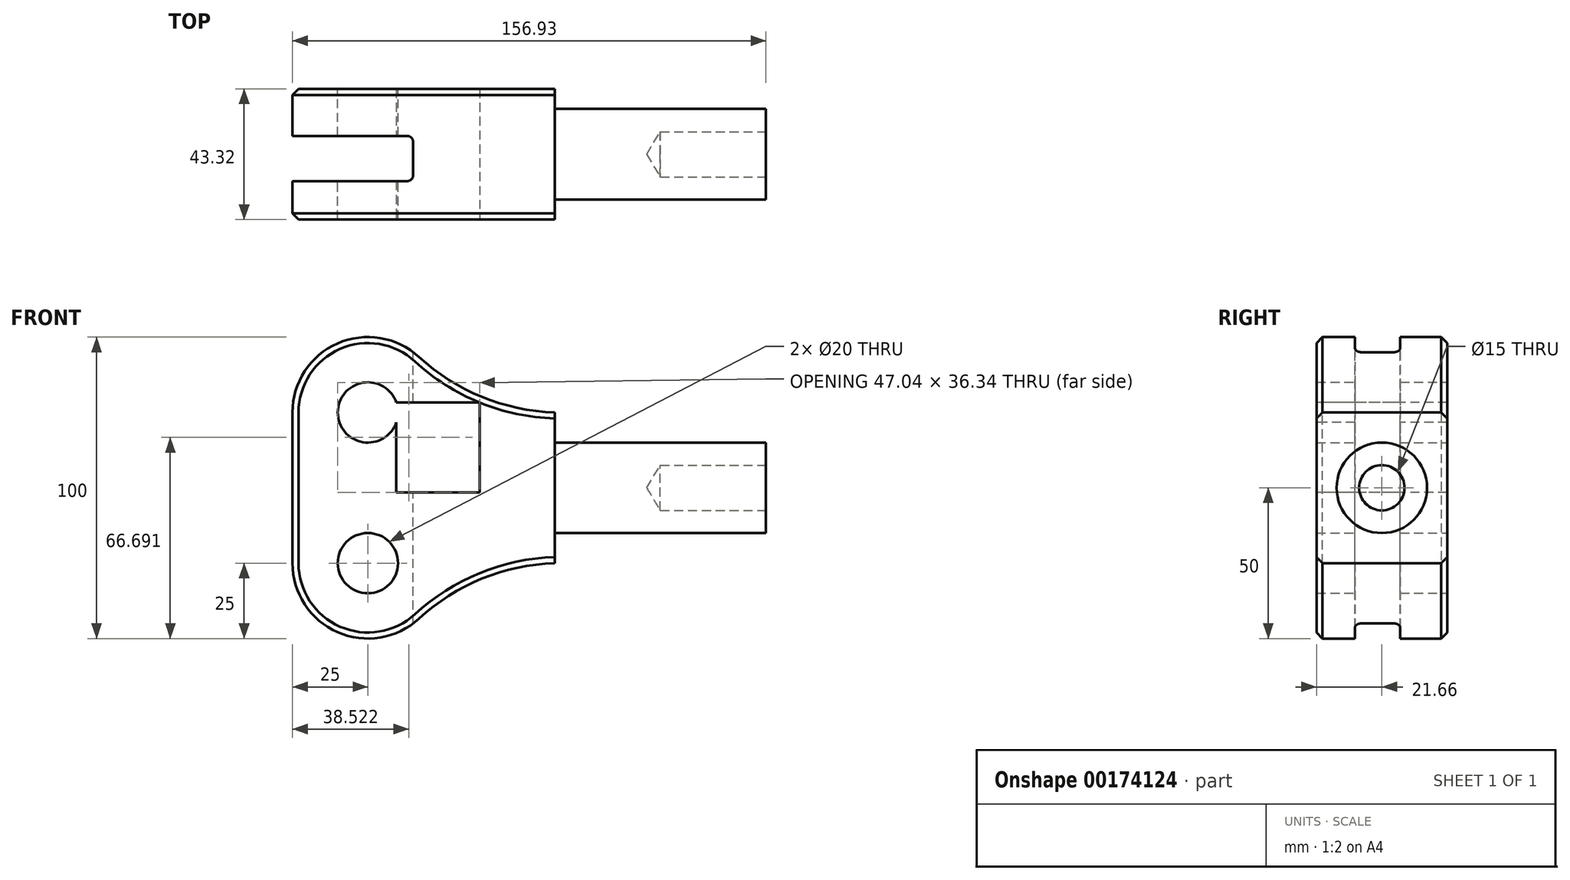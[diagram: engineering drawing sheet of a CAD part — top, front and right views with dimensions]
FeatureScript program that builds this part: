
annotation { "Feature Type Name" : "Feature", "Feature Type Description" : "" }
export const myFeature = defineFeature(function(context is Context, id is Id, definition is map)
    precondition{}
    {
        {
            var Q0;
            Q0=qCreatedBy(makeId("Front.planeOp"),FACE);
            var sketch = newSketch(context, id + "F9", { "sketchPlane" : qUnion([Q0])});
            skLineSegment(sketch, "E0.bottom", {"start": v(0, 0) * mm, "end": v(0, 0) * mm});
            skLineSegment(sketch, "E0.top", {"start": v(0, 0) * mm, "end": v(0, 0) * mm});
            skLineSegment(sketch, "E0.left", {"start": v(0, 0) * mm, "end": v(0, 0) * mm});
            skLineSegment(sketch, "E0.right", {"start": v(0, 0) * mm, "end": v(0, 0) * mm});
            skPoint(sketch, "E0.middle", {"position": v(0, 0) * mm});
            skLineSegment(sketch, "E1.left", {"start": v(0, 0) * mm, "end": v(0, 50) * mm});
            skLineSegment(sketch, "E1.right", {"start": v(50, 0) * mm, "end": v(50, 50) * mm});
            skArc(sketch, "E2", {"start": v(0, 0) * mm, "mid": v(25, -25) * mm, "end": v(50, 0) * mm});
            skArc(sketch, "E3", {"start": v(50, 50) * mm, "mid": v(25, 75) * mm, "end": v(0, 50) * mm});
            skLineSegment(sketch, "E4.bottom", {"start": v(50, 0) * mm, "end": v(86.93, 0) * mm});
            skLineSegment(sketch, "E4.top", {"start": v(50, 50) * mm, "end": v(86.93, 50) * mm});
            skLineSegment(sketch, "E4.right", {"start": v(86.93, 0) * mm, "end": v(86.93, 50) * mm});
            skCircle(sketch, "E5", {"center": v(25, 0) * mm, "radius": 10 * mm});
            skCircle(sketch, "E6", {"center": v(25, 50) * mm, "radius": 10 * mm});
            skSolve(sketch);
        }
        {
            var Q0;
            Q0=makeQuery(id+"F9.imprint","IMPRINT",FACE,{"disambiguationData":[TD([[makeQuery(id+"F9.imprint","IMPRINT",EDGE,{"derivedFrom":sQuery(id+"F9.wireOp",EDGE,"E1.left")}),-1.0]])]});
            var Q1;
            Q1=makeQuery(id+"F9.imprint","IMPRINT",FACE,{"disambiguationData":[TD([[makeQuery(id+"F9.imprint","IMPRINT",EDGE,{"derivedFrom":sQuery(id+"F9.wireOp",EDGE,"E4.bottom")}),1.0]])]});
            extrude(context, id + "F0", {"entities" : qUnion([Q0, Q1]), "depth" : 43.32 * mm});
        }
        {
            var Q0;
            Q0=makeQuery(id+"F0.opExtrude","SWEPT_FACE",FACE,{"disambiguationData":[OSD([sQuery(id+"F9.wireOp",EDGE,"E1.left")])]});
            var sketch = newSketch(context, id + "F10", { "sketchPlane" : qUnion([Q0])});
            skSolve(sketch);
        }
        {
            var Q0;
            {var subQ0=sQuery(id+"F9.wireOp",EDGE,"E1.left");Q0=makeQuery(id+"F10.imprint","IMPRINT",FACE,{"disambiguationData":[TD([[makeQuery(id+"F10.imprint","IMPRINT",EDGE,{"derivedFrom":makeQuery(id+"F0.opExtrude","CAP_EDGE",EDGE,{"disambiguationData":[OSD([subQ0])],"isStart":true})}),-1.0]])]});}
            var sketch = newSketch(context, id + "F1", { "sketchPlane" : qUnion([Q0])});
            skLineSegment(sketch, "E7.bottom", {"start": v(15.58, -37.24) * mm, "end": v(30.58, -37.24) * mm});
            skLineSegment(sketch, "E7.top", {"start": v(15.58, 86.12) * mm, "end": v(30.58, 86.12) * mm});
            skLineSegment(sketch, "E7.left", {"start": v(15.58, -37.24) * mm, "end": v(15.58, 86.12) * mm});
            skLineSegment(sketch, "E7.right", {"start": v(30.58, -37.24) * mm, "end": v(30.58, 86.12) * mm});
            skLineSegment(sketch, "E8", {"start": v(24.84, -78.93) * mm, "end": v(24.84, 88.44) * mm, "construction": true});
            skSolve(sketch);
        }
        {
            var Q0;
            {var subQ0=sQuery(id+"F1.wireOp",EDGE,"E7.top");Q0=makeQuery(id+"F1.imprint","IMPRINT",FACE,{"disambiguationData":[TD([[makeQuery(id+"F1.imprint","IMPRINT",EDGE,{"derivedFrom":subQ0}),-1.0]])]});}
            var Q1;
            {var subQ0=sQuery(id+"F1.wireOp",EDGE,"E7.bottom");Q1=makeQuery(id+"F1.imprint","IMPRINT",FACE,{"disambiguationData":[TD([[makeQuery(id+"F1.imprint","IMPRINT",EDGE,{"derivedFrom":subQ0}),1.0]])]});}
            var Q2;
            {var subQ0=sQuery(id+"F1.wireOp",EDGE,"E7.left");var subQ1=sQuery(id+"F9.wireOp",EDGE,"E1.left");var subQ2=makeQuery(id+"F10.imprint","IMPRINT",EDGE,{"derivedFrom":makeQuery(id+"F0.opExtrude","SWEPT_EDGE",EDGE,{"disambiguationData":[OSD([subQ1,sQuery(id+"F9.wireOp",EDGE,"E2")])]})});var subQ3=makeQuery(id+"F1.imprint","INTERSECT",VERTEX,{"derivedFrom":[subQ2,subQ0]});Q2=makeQuery(id+"F1.imprint","IMPRINT",FACE,{"disambiguationData":[TD([[makeQuery(id+"F1.imprint","IMPRINT",EDGE,{"disambiguationData":[TD([[subQ3,-1.0]])],"derivedFrom":subQ0}),-1.0]])]});}
            extrude(context, id + "F11", {"entities" : qUnion([Q0, Q1, Q2]), "operationType" : NewBodyOperationType.REMOVE, "oppositeDirection" : true, "depth" : 40 * mm});
        }
        {
            var Q0;
            Q0=makeQuery(id+"F0.opExtrude","SWEPT_EDGE",EDGE,{"disambiguationData":[OSD([sQuery(id+"F9.wireOp",EDGE,"E3"),sQuery(id+"F9.wireOp",EDGE,"E4.top"),sQuery(id+"F9.wireOp",EDGE,"E1.right")])]});
            var Q1;
            Q1=makeQuery(id+"F0.opExtrude","SWEPT_EDGE",EDGE,{"disambiguationData":[OSD([sQuery(id+"F9.wireOp",EDGE,"E2"),sQuery(id+"F9.wireOp",EDGE,"E4.bottom"),sQuery(id+"F9.wireOp",EDGE,"E1.right")])]});
            fillet(context, id + "F2", {"entities" : qUnion([Q0, Q1]), "radius" : 70 * mm, "tangentPropagation" : true, "allowEdgeOverflow" : false});
        }
        {
            var Q0;
            Q0=makeQuery(id+"F0.opExtrude","SWEPT_FACE",FACE,{"disambiguationData":[OSD([sQuery(id+"F9.wireOp",EDGE,"E4.right")])]});
            var sketch = newSketch(context, id + "F12", { "sketchPlane" : qUnion([Q0])});
            skCircle(sketch, "E9", {"center": v(-21.66, 25) * mm, "radius": 15 * mm});
            skPoint(sketch, "E9.centerSnap0", {"position": v(-21.66, 0) * mm});
            skPoint(sketch, "E9.centerSnap1", {"position": v(0, 25) * mm});
            skSolve(sketch);
        }
        {
            var Q0;
            Q0=makeQuery(id+"F12.imprint","IMPRINT",FACE,{"disambiguationData":[TD([[makeQuery(id+"F12.imprint","IMPRINT",EDGE,{"derivedFrom":sQuery(id+"F12.wireOp",EDGE,"E9")}),1.0]])]});
            extrude(context, id + "F3", {"entities" : qUnion([Q0]), "operationType" : NewBodyOperationType.ADD, "depth" : 70 * mm});
        }
        {
            var Q0;
            Q0=makeQuery(id+"F3.opExtrude","CAP_FACE",FACE,{"disambiguationData":[OSD([sQuery(id+"F12.wireOp",EDGE,"E9")])],"isStart":false});
            var sketch = newSketch(context, id + "F13", { "sketchPlane" : qUnion([Q0])});
            skPoint(sketch, "E10", {"position": v(-21.66, 25) * mm});
            skSolve(sketch);
        }
        {
            var Q0;
            Q0=sQuery(id+"F13.wireOp",VERTEX,"E10");
            var Q1;
            Q1=makeQuery(id+"F0.opExtrude","SWEPT_BODY",BODY,{"disambiguationData":[OSD([sQuery(id+"F9.wireOp",EDGE,"E1.left"),sQuery(id+"F9.wireOp",EDGE,"E2"),sQuery(id+"F9.wireOp",EDGE,"E3"),sQuery(id+"F9.wireOp",EDGE,"E4.bottom"),sQuery(id+"F9.wireOp",EDGE,"E4.top"),sQuery(id+"F9.wireOp",EDGE,"E4.right"),sQuery(id+"F9.wireOp",EDGE,"E5"),sQuery(id+"F9.wireOp",EDGE,"E6")])]});
            hole(context, id + "F4", {"style" : HoleStyle.SIMPLE, "endStyle" : HoleEndStyle.BLIND, "holeDiameter" : 15 * mm, "holeDepth" : 35 * mm, "locations" : qUnion([Q0]), "scope" : qUnion([Q1])});
        }
        {
            var Q0;
            Q0=makeQuery(id+"F0.opExtrude","CAP_EDGE",EDGE,{"disambiguationData":[OSD([sQuery(id+"F9.wireOp",EDGE,"E1.left")])],"isStart":true});
            var Q1;
            Q1=makeQuery(id+"F0.opExtrude","CAP_EDGE",EDGE,{"disambiguationData":[OSD([sQuery(id+"F9.wireOp",EDGE,"E3")])],"isStart":true});
            var Q2;
            Q2=makeQuery(id+"F0.opExtrude","CAP_EDGE",EDGE,{"disambiguationData":[OSD([sQuery(id+"F9.wireOp",EDGE,"E2")])],"isStart":true});
            var Q3;
            {var subQ0=sQuery(id+"F9.wireOp",EDGE,"E4.bottom");var subQ1=sQuery(id+"F9.wireOp",EDGE,"E2");Q3=makeQuery(id+"F2.opFillet","BLEND_EDGE",EDGE,{"blendedFrom":[makeQuery(id+"F0.opExtrude","SWEPT_EDGE",EDGE,{"disambiguationData":[OSD([subQ1,subQ0,sQuery(id+"F9.wireOp",EDGE,"E1.right")])]}),makeQuery(id+"F0.opExtrude","CAP_FACE",FACE,{"disambiguationData":[OSD([sQuery(id+"F9.wireOp",EDGE,"E1.left"),subQ1,sQuery(id+"F9.wireOp",EDGE,"E3"),subQ0,sQuery(id+"F9.wireOp",EDGE,"E4.top"),sQuery(id+"F9.wireOp",EDGE,"E4.right"),sQuery(id+"F9.wireOp",EDGE,"E5"),sQuery(id+"F9.wireOp",EDGE,"E6")])],"isStart":true})],"blendedInto":[makeQuery(id+"F0.opExtrude","CAP_FACE",FACE,{"disambiguationData":[OSD([sQuery(id+"F9.wireOp",EDGE,"E1.left"),subQ1,sQuery(id+"F9.wireOp",EDGE,"E3"),subQ0,sQuery(id+"F9.wireOp",EDGE,"E4.top"),sQuery(id+"F9.wireOp",EDGE,"E4.right"),sQuery(id+"F9.wireOp",EDGE,"E5"),sQuery(id+"F9.wireOp",EDGE,"E6")])],"isStart":true})]});}
            var Q4;
            {var subQ0=sQuery(id+"F9.wireOp",EDGE,"E4.top");var subQ1=sQuery(id+"F9.wireOp",EDGE,"E3");Q4=makeQuery(id+"F2.opFillet","BLEND_EDGE",EDGE,{"blendedFrom":[makeQuery(id+"F0.opExtrude","SWEPT_EDGE",EDGE,{"disambiguationData":[OSD([subQ1,subQ0,sQuery(id+"F9.wireOp",EDGE,"E1.right")])]}),makeQuery(id+"F0.opExtrude","CAP_FACE",FACE,{"disambiguationData":[OSD([sQuery(id+"F9.wireOp",EDGE,"E1.left"),sQuery(id+"F9.wireOp",EDGE,"E2"),subQ1,sQuery(id+"F9.wireOp",EDGE,"E4.bottom"),subQ0,sQuery(id+"F9.wireOp",EDGE,"E4.right"),sQuery(id+"F9.wireOp",EDGE,"E5"),sQuery(id+"F9.wireOp",EDGE,"E6")])],"isStart":true})],"blendedInto":[makeQuery(id+"F0.opExtrude","CAP_FACE",FACE,{"disambiguationData":[OSD([sQuery(id+"F9.wireOp",EDGE,"E1.left"),sQuery(id+"F9.wireOp",EDGE,"E2"),subQ1,sQuery(id+"F9.wireOp",EDGE,"E4.bottom"),subQ0,sQuery(id+"F9.wireOp",EDGE,"E4.right"),sQuery(id+"F9.wireOp",EDGE,"E5"),sQuery(id+"F9.wireOp",EDGE,"E6")])],"isStart":true})]});}
            var Q5;
            Q5=makeQuery(id+"F0.opExtrude","CAP_EDGE",EDGE,{"disambiguationData":[OSD([sQuery(id+"F9.wireOp",EDGE,"E1.left")])],"isStart":false});
            var Q6;
            Q6=makeQuery(id+"F0.opExtrude","CAP_EDGE",EDGE,{"disambiguationData":[OSD([sQuery(id+"F9.wireOp",EDGE,"E3")])],"isStart":false});
            var Q7;
            {var subQ0=sQuery(id+"F9.wireOp",EDGE,"E4.top");var subQ1=sQuery(id+"F9.wireOp",EDGE,"E3");Q7=makeQuery(id+"F2.opFillet","BLEND_EDGE",EDGE,{"blendedFrom":[makeQuery(id+"F0.opExtrude","SWEPT_EDGE",EDGE,{"disambiguationData":[OSD([subQ1,subQ0,sQuery(id+"F9.wireOp",EDGE,"E1.right")])]}),makeQuery(id+"F0.opExtrude","CAP_FACE",FACE,{"disambiguationData":[OSD([sQuery(id+"F9.wireOp",EDGE,"E1.left"),sQuery(id+"F9.wireOp",EDGE,"E2"),subQ1,sQuery(id+"F9.wireOp",EDGE,"E4.bottom"),subQ0,sQuery(id+"F9.wireOp",EDGE,"E4.right"),sQuery(id+"F9.wireOp",EDGE,"E5"),sQuery(id+"F9.wireOp",EDGE,"E6")])],"isStart":false})],"blendedInto":[makeQuery(id+"F0.opExtrude","CAP_FACE",FACE,{"disambiguationData":[OSD([sQuery(id+"F9.wireOp",EDGE,"E1.left"),sQuery(id+"F9.wireOp",EDGE,"E2"),subQ1,sQuery(id+"F9.wireOp",EDGE,"E4.bottom"),subQ0,sQuery(id+"F9.wireOp",EDGE,"E4.right"),sQuery(id+"F9.wireOp",EDGE,"E5"),sQuery(id+"F9.wireOp",EDGE,"E6")])],"isStart":false})]});}
            var Q8;
            Q8=makeQuery(id+"F0.opExtrude","CAP_EDGE",EDGE,{"disambiguationData":[OSD([sQuery(id+"F9.wireOp",EDGE,"E2")])],"isStart":false});
            var Q9;
            {var subQ0=sQuery(id+"F9.wireOp",EDGE,"E4.bottom");var subQ1=sQuery(id+"F9.wireOp",EDGE,"E2");Q9=makeQuery(id+"F2.opFillet","BLEND_EDGE",EDGE,{"blendedFrom":[makeQuery(id+"F0.opExtrude","SWEPT_EDGE",EDGE,{"disambiguationData":[OSD([subQ1,subQ0,sQuery(id+"F9.wireOp",EDGE,"E1.right")])]}),makeQuery(id+"F0.opExtrude","CAP_FACE",FACE,{"disambiguationData":[OSD([sQuery(id+"F9.wireOp",EDGE,"E1.left"),subQ1,sQuery(id+"F9.wireOp",EDGE,"E3"),subQ0,sQuery(id+"F9.wireOp",EDGE,"E4.top"),sQuery(id+"F9.wireOp",EDGE,"E4.right"),sQuery(id+"F9.wireOp",EDGE,"E5"),sQuery(id+"F9.wireOp",EDGE,"E6")])],"isStart":false})],"blendedInto":[makeQuery(id+"F0.opExtrude","CAP_FACE",FACE,{"disambiguationData":[OSD([sQuery(id+"F9.wireOp",EDGE,"E1.left"),subQ1,sQuery(id+"F9.wireOp",EDGE,"E3"),subQ0,sQuery(id+"F9.wireOp",EDGE,"E4.top"),sQuery(id+"F9.wireOp",EDGE,"E4.right"),sQuery(id+"F9.wireOp",EDGE,"E5"),sQuery(id+"F9.wireOp",EDGE,"E6")])],"isStart":false})]});}
            chamfer(context, id + "F5", {"entities" : qUnion([Q0, Q1, Q2, Q3, Q4, Q5, Q6, Q7, Q8, Q9]), "width" : 2 * mm, "tangentPropagation" : true});
        }
        {
            var Q0;
            Q0=makeQuery(id+"F11.boolean.opBoolean","COPY",EDGE,{"derivedFrom":makeQuery(id+"F11.opExtrude","CAP_EDGE",EDGE,{"disambiguationData":[OSD([sQuery(id+"F1.wireOp",EDGE,"E7.right")])],"isStart":false})});
            var Q1;
            Q1=makeQuery(id+"F11.boolean.opBoolean","COPY",EDGE,{"derivedFrom":makeQuery(id+"F11.opExtrude","CAP_EDGE",EDGE,{"disambiguationData":[OSD([sQuery(id+"F1.wireOp",EDGE,"E7.left")])],"isStart":false})});
            fillet(context, id + "F6", {"entities" : qUnion([Q0, Q1]), "radius" : 2 * mm, "tangentPropagation" : true, "allowEdgeOverflow" : false});
        }
        {
            var Q0;
            Q0=makeQuery(id+"F0.opExtrude","CAP_FACE",FACE,{"disambiguationData":[OSD([sQuery(id+"F9.wireOp",EDGE,"E1.left"),sQuery(id+"F9.wireOp",EDGE,"E2"),sQuery(id+"F9.wireOp",EDGE,"E3"),sQuery(id+"F9.wireOp",EDGE,"E4.bottom"),sQuery(id+"F9.wireOp",EDGE,"E4.top"),sQuery(id+"F9.wireOp",EDGE,"E4.right"),sQuery(id+"F9.wireOp",EDGE,"E5"),sQuery(id+"F9.wireOp",EDGE,"E6")])],"isStart":false});
            var sketch = newSketch(context, id + "F7", { "sketchPlane" : qUnion([Q0])});
            skPoint(sketch, "E11.firstSnap0", {"position": v(62.04, 53.3) * mm});
            skPoint(sketch, "E11.oppositeSnap0", {"position": v(62.04, 53.3) * mm});
            skLineSegment(sketch, "E11.bottom", {"start": v(34.44, 53.3) * mm, "end": v(62.04, 53.3) * mm});
            skLineSegment(sketch, "E11.top", {"start": v(34.44, 23.52) * mm, "end": v(62.04, 23.52) * mm});
            skLineSegment(sketch, "E11.left", {"start": v(34.44, 53.3) * mm, "end": v(34.44, 23.52) * mm});
            skLineSegment(sketch, "E11.right", {"start": v(62.04, 53.3) * mm, "end": v(62.04, 23.52) * mm});
            skSolve(sketch);
        }
        {
            var Q0;
            {var subQ4=sQuery(id+"F7.wireOp",EDGE,"E11.bottom");Q0=makeQuery(id+"F7.imprint","IMPRINT",FACE,{"disambiguationData":[TD([[makeQuery(id+"F7.imprint","IMPRINT",EDGE,{"derivedFrom":subQ4}),-1.0]])]});}
            extrude(context, id + "F8", {"entities" : qUnion([Q0]), "operationType" : NewBodyOperationType.REMOVE, "oppositeDirection" : true, "depth" : 66.83 * mm});
        }
    });
